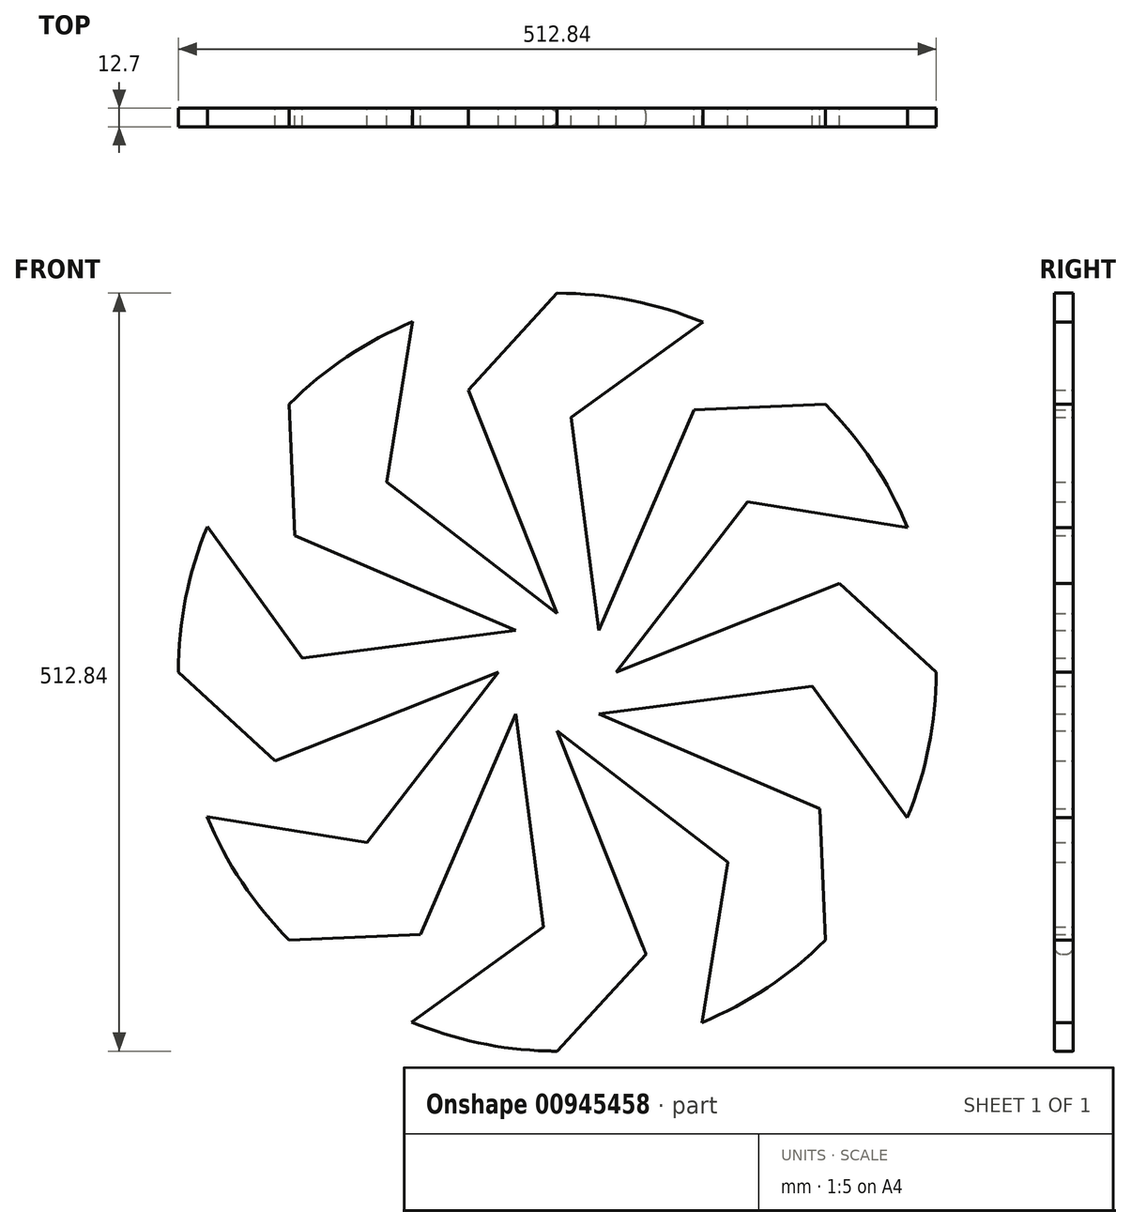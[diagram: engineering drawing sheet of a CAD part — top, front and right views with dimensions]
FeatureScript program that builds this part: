
annotation { "Feature Type Name" : "Feature", "Feature Type Description" : "" }
export const myFeature = defineFeature(function(context is Context, id is Id, definition is map)
    precondition{}
    {
        {
            var Q0;
            Q0=qCreatedBy(makeId("Front.planeOp"),FACE);
            var sketch = newSketch(context, id + "F0", { "sketchPlane" : qUnion([Q0])});
            skArc(sketch, "E0", {"start": v(-97.8, 237.03) * mm, "mid": v(-142.31, 213.3) * mm, "end": v(-181.31, 181.31) * mm});
            skLineSegment(sketch, "E1", {"start": v(-28.15, 28.15) * mm, "end": v(-177.52, 92.54) * mm});
            skLineSegment(sketch, "E2", {"start": v(-177.52, 92.54) * mm, "end": v(-181.31, 181.31) * mm});
            skLineSegment(sketch, "E3", {"start": v(0, 39.8) * mm, "end": v(-115.26, 128.69) * mm});
            skLineSegment(sketch, "E4", {"start": v(-115.26, 128.69) * mm, "end": v(-97.8, 237.03) * mm});
            skLineSegment(sketch, "E5.1.0", {"start": v(-39.8, 0) * mm, "end": v(-190.96, -60.1) * mm});
            skLineSegment(sketch, "E5.1.1", {"start": v(-28.15, 28.15) * mm, "end": v(-172.5, 9.5) * mm});
            skLineSegment(sketch, "E5.1.2", {"start": v(-172.5, 9.5) * mm, "end": v(-236.76, 98.45) * mm});
            skLineSegment(sketch, "E5.1.3", {"start": v(-190.96, -60.1) * mm, "end": v(-256.42, 0) * mm});
            skLineSegment(sketch, "E5.2.0", {"start": v(-28.15, -28.15) * mm, "end": v(-92.54, -177.52) * mm});
            skLineSegment(sketch, "E5.2.1", {"start": v(-39.8, 0) * mm, "end": v(-128.69, -115.26) * mm});
            skLineSegment(sketch, "E5.2.2", {"start": v(-128.69, -115.26) * mm, "end": v(-237.03, -97.8) * mm});
            skLineSegment(sketch, "E5.2.3", {"start": v(-92.54, -177.52) * mm, "end": v(-181.31, -181.31) * mm});
            skLineSegment(sketch, "E5.3.0", {"start": v(0, -39.8) * mm, "end": v(60.1, -190.96) * mm});
            skLineSegment(sketch, "E5.3.1", {"start": v(-28.15, -28.15) * mm, "end": v(-9.5, -172.5) * mm});
            skLineSegment(sketch, "E5.3.2", {"start": v(-9.5, -172.5) * mm, "end": v(-98.45, -236.76) * mm});
            skLineSegment(sketch, "E5.3.3", {"start": v(60.1, -190.96) * mm, "end": v(0, -256.42) * mm});
            skLineSegment(sketch, "E5.4.0", {"start": v(28.15, -28.15) * mm, "end": v(177.52, -92.54) * mm});
            skLineSegment(sketch, "E5.4.1", {"start": v(0, -39.8) * mm, "end": v(115.26, -128.69) * mm});
            skLineSegment(sketch, "E5.4.2", {"start": v(115.26, -128.69) * mm, "end": v(97.8, -237.03) * mm});
            skLineSegment(sketch, "E5.4.3", {"start": v(177.52, -92.54) * mm, "end": v(181.31, -181.31) * mm});
            skLineSegment(sketch, "E5.5.0", {"start": v(39.8, 0) * mm, "end": v(190.96, 60.1) * mm});
            skLineSegment(sketch, "E5.5.1", {"start": v(28.15, -28.15) * mm, "end": v(172.5, -9.5) * mm});
            skLineSegment(sketch, "E5.5.2", {"start": v(172.5, -9.5) * mm, "end": v(236.76, -98.45) * mm});
            skLineSegment(sketch, "E5.5.3", {"start": v(190.96, 60.1) * mm, "end": v(256.42, 0) * mm});
            skLineSegment(sketch, "E5.6.0", {"start": v(28.15, 28.15) * mm, "end": v(92.54, 177.52) * mm});
            skLineSegment(sketch, "E5.6.1", {"start": v(39.8, 0) * mm, "end": v(128.69, 115.26) * mm});
            skLineSegment(sketch, "E5.6.2", {"start": v(128.69, 115.26) * mm, "end": v(237.03, 97.8) * mm});
            skLineSegment(sketch, "E5.6.3", {"start": v(92.54, 177.52) * mm, "end": v(181.31, 181.31) * mm});
            skLineSegment(sketch, "E5.7.0", {"start": v(0, 39.8) * mm, "end": v(-60.1, 190.96) * mm});
            skLineSegment(sketch, "E5.7.1", {"start": v(28.15, 28.15) * mm, "end": v(9.5, 172.5) * mm});
            skLineSegment(sketch, "E5.7.2", {"start": v(9.5, 172.5) * mm, "end": v(98.45, 236.76) * mm});
            skLineSegment(sketch, "E5.7.3", {"start": v(-60.1, 190.96) * mm, "end": v(0, 256.42) * mm});
            skArc(sketch, "E6.trimOffspring", {"start": v(-236.76, 98.45) * mm, "mid": v(-251.46, 50.2) * mm, "end": v(-256.42, 0) * mm});
            skArc(sketch, "E7.trimOffspring", {"start": v(-237.03, -97.8) * mm, "mid": v(-213.3, -142.31) * mm, "end": v(-181.31, -181.31) * mm});
            skArc(sketch, "E8.trimOffspring", {"start": v(-98.45, -236.76) * mm, "mid": v(-50.2, -251.46) * mm, "end": v(0, -256.42) * mm});
            skArc(sketch, "E9.trimOffspring", {"start": v(97.8, -237.03) * mm, "mid": v(142.31, -213.3) * mm, "end": v(181.31, -181.31) * mm});
            skArc(sketch, "E10.trimOffspring", {"start": v(236.76, -98.45) * mm, "mid": v(251.46, -50.2) * mm, "end": v(256.42, 0) * mm});
            skArc(sketch, "E11.trimOffspring", {"start": v(237.03, 97.8) * mm, "mid": v(213.3, 142.31) * mm, "end": v(181.31, 181.31) * mm});
            skArc(sketch, "E12.trimOffspring", {"start": v(98.45, 236.76) * mm, "mid": v(50.2, 251.46) * mm, "end": v(0, 256.42) * mm});
            skSolve(sketch);
        }
        {
            var Q0;
            Q0 = qSketchRegion(id + "F0", true);
            extrude(context, id + "F1", {"entities" : qUnion([Q0]), "depth" : 12.7 * mm, "offsetDistance" : 25.4 * mm});
        }
        {
            var Q0;
            Q0=makeQuery(id+"F1.opExtrude","CAP_EDGE",EDGE,{"disambiguationData":[OSD([sQuery(id+"F0.wireOp",EDGE,"E5.3.3")])],"isStart":false});
            var Q1;
            Q1=makeQuery(id+"F1.opExtrude","CAP_EDGE",EDGE,{"disambiguationData":[OSD([sQuery(id+"F0.wireOp",EDGE,"E5.3.3")])],"isStart":true});
            fillet(context, id + "F2", {"entities" : qUnion([Q0, Q1]), "radius" : 5.08 * mm, "tangentPropagation" : true, "allowEdgeOverflow" : false});
        }
    });
